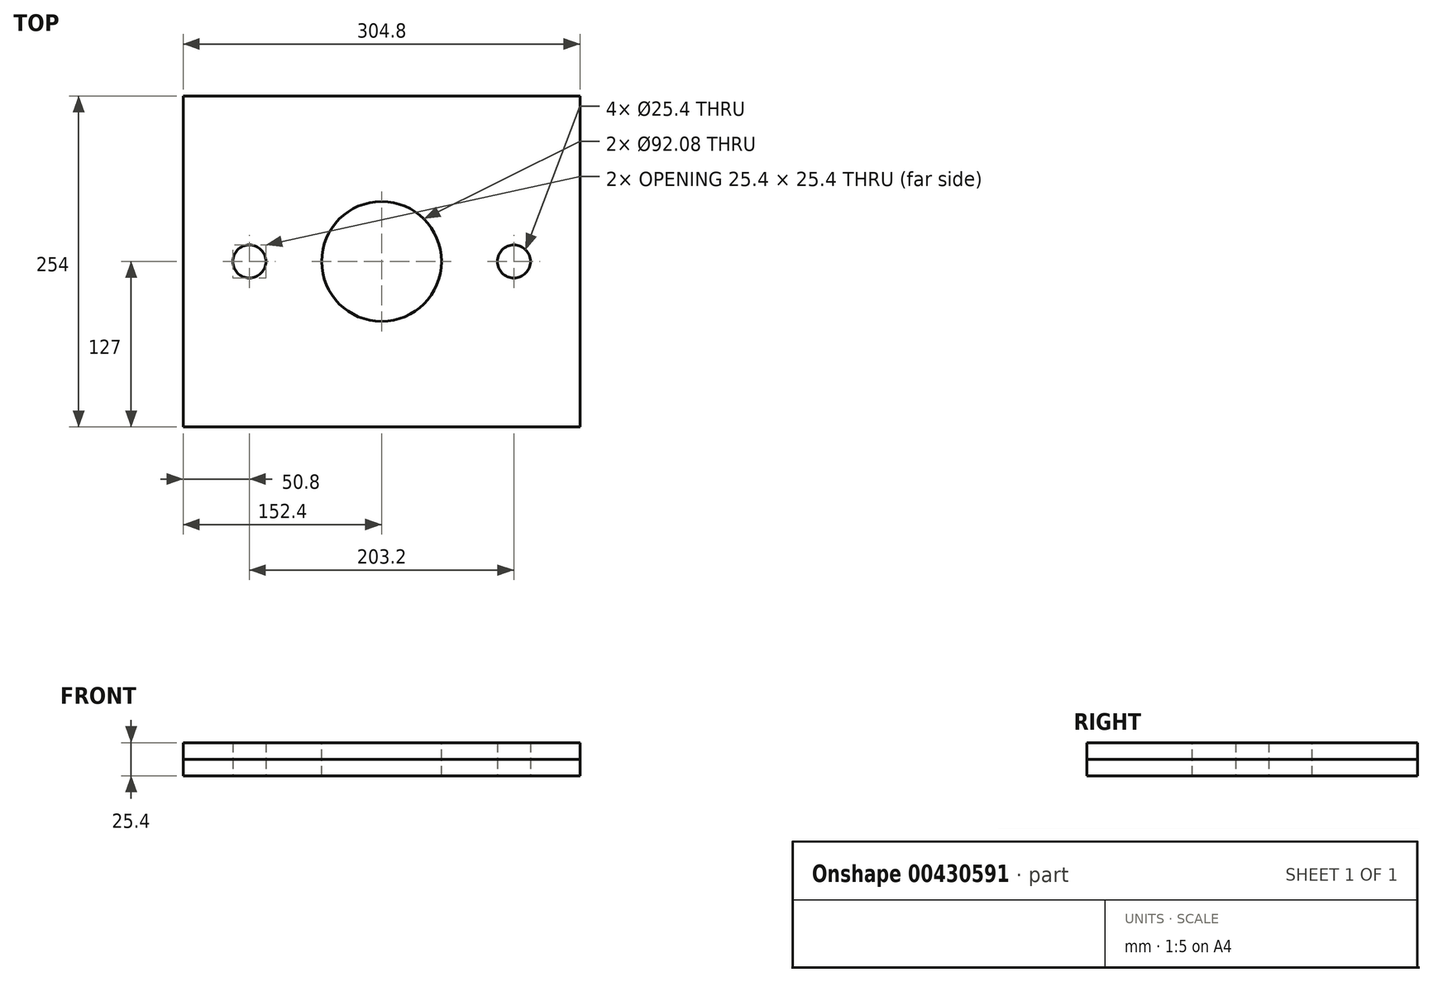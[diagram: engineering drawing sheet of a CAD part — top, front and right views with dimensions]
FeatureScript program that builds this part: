
annotation { "Feature Type Name" : "Feature", "Feature Type Description" : "" }
export const myFeature = defineFeature(function(context is Context, id is Id, definition is map)
    precondition{}
    {
        {
            var Q0;
            Q0=qCreatedBy(makeId("Top.planeOp"),FACE);
            var sketch = newSketch(context, id + "F0", { "sketchPlane" : qUnion([Q0])});
            skLineSegment(sketch, "E0.bottom", {"start": v(152.4, -127) * mm, "end": v(-152.4, -127) * mm});
            skLineSegment(sketch, "E0.top", {"start": v(152.4, 127) * mm, "end": v(-152.4, 127) * mm});
            skLineSegment(sketch, "E0.left", {"start": v(152.4, -127) * mm, "end": v(152.4, 127) * mm});
            skLineSegment(sketch, "E0.right", {"start": v(-152.4, -127) * mm, "end": v(-152.4, 127) * mm});
            skPoint(sketch, "E0.middle", {"position": v(0, 0) * mm});
            skSolve(sketch);
        }
        {
            var Q0;
            Q0=makeQuery(id+"F0.imprint","IMPRINT",FACE,{"disambiguationData":[TD([[makeQuery(id+"F0.imprint","IMPRINT",EDGE,{"derivedFrom":sQuery(id+"F0.wireOp",EDGE,"E0.bottom")}),-1.0]])]});
            extrude(context, id + "F1", {"entities" : qUnion([Q0]), "endBound" : BoundingType.SYMMETRIC, "depth" : 12.7 * mm});
        }
        {
            var Q0;
            Q0=makeQuery(id+"F1.opExtrude","CAP_FACE",FACE,{"disambiguationData":[OSD([sQuery(id+"F0.wireOp",EDGE,"E0.bottom"),sQuery(id+"F0.wireOp",EDGE,"E0.top"),sQuery(id+"F0.wireOp",EDGE,"E0.left"),sQuery(id+"F0.wireOp",EDGE,"E0.right")])],"isStart":false});
            extrude(context, id + "F2", {"entities" : qUnion([Q0]), "depth" : 12.7 * mm});
        }
        {
            var Q0;
            Q0=makeQuery(id+"F2.opExtrude","CAP_FACE",FACE,{"disambiguationData":[OSD([sQuery(id+"F0.wireOp",EDGE,"E0.bottom"),sQuery(id+"F0.wireOp",EDGE,"E0.top"),sQuery(id+"F0.wireOp",EDGE,"E0.left"),sQuery(id+"F0.wireOp",EDGE,"E0.right")])],"isStart":false});
            var sketch = newSketch(context, id + "F3", { "sketchPlane" : qUnion([Q0])});
            skCircle(sketch, "E1", {"center": v(0, 0) * mm, "radius": 46.04 * mm});
            skSolve(sketch);
        }
        {
            var Q0;
            Q0 = qSketchRegion(id + "F3", true);
            extrude(context, id + "F4", {"entities" : qUnion([Q0]), "operationType" : NewBodyOperationType.REMOVE, "endBound" : BoundingType.THROUGH_ALL, "oppositeDirection" : true, "depth" : 25.4 * mm});
        }
        {
            var Q0;
            Q0=makeQuery(id+"F1.opExtrude","CAP_FACE",FACE,{"disambiguationData":[OSD([sQuery(id+"F0.wireOp",EDGE,"E0.bottom"),sQuery(id+"F0.wireOp",EDGE,"E0.top"),sQuery(id+"F0.wireOp",EDGE,"E0.left"),sQuery(id+"F0.wireOp",EDGE,"E0.right")])],"isStart":true});
            var sketch = newSketch(context, id + "F5", { "sketchPlane" : qUnion([Q0])});
            skCircle(sketch, "E2", {"center": v(-101.6, 0) * mm, "radius": 12.7 * mm});
            skCircle(sketch, "E3", {"center": v(101.6, 0) * mm, "radius": 12.7 * mm});
            skSolve(sketch);
        }
        {
            var Q0;
            Q0 = qSketchRegion(id + "F5", true);
            extrude(context, id + "F6", {"entities" : qUnion([Q0]), "operationType" : NewBodyOperationType.REMOVE, "oppositeDirection" : true, "depth" : 25.4 * mm});
        }
        {
            var Q0;
            Q0=makeQuery(id+"F2.opExtrude","CAP_FACE",FACE,{"disambiguationData":[OSD([sQuery(id+"F0.wireOp",EDGE,"E0.bottom"),sQuery(id+"F0.wireOp",EDGE,"E0.top"),sQuery(id+"F0.wireOp",EDGE,"E0.left"),sQuery(id+"F0.wireOp",EDGE,"E0.right")])],"isStart":false});
            var sketch = newSketch(context, id + "F7", { "sketchPlane" : qUnion([Q0])});
            skCircle(sketch, "E4", {"center": v(-101.6, 0) * mm, "radius": 3.18 * mm});
            skCircle(sketch, "E5", {"center": v(101.6, 0) * mm, "radius": 3.18 * mm});
            skSolve(sketch);
        }
        {
            var Q0;
            Q0=makeQuery(id+"F7.imprint","IMPRINT",FACE,{"disambiguationData":[TD([[makeQuery(id+"F7.imprint","IMPRINT",EDGE,{"derivedFrom":sQuery(id+"F7.wireOp",EDGE,"E4")}),1.0]])]});
            var Q1;
            Q1=makeQuery(id+"F7.imprint","IMPRINT",FACE,{"disambiguationData":[TD([[makeQuery(id+"F7.imprint","IMPRINT",EDGE,{"derivedFrom":sQuery(id+"F7.wireOp",EDGE,"E5")}),1.0]])]});
            extrude(context, id + "F8", {"entities" : qUnion([Q0, Q1]), "operationType" : NewBodyOperationType.REMOVE, "endBound" : BoundingType.THROUGH_ALL, "oppositeDirection" : true, "depth" : 25.4 * mm});
        }
    });
